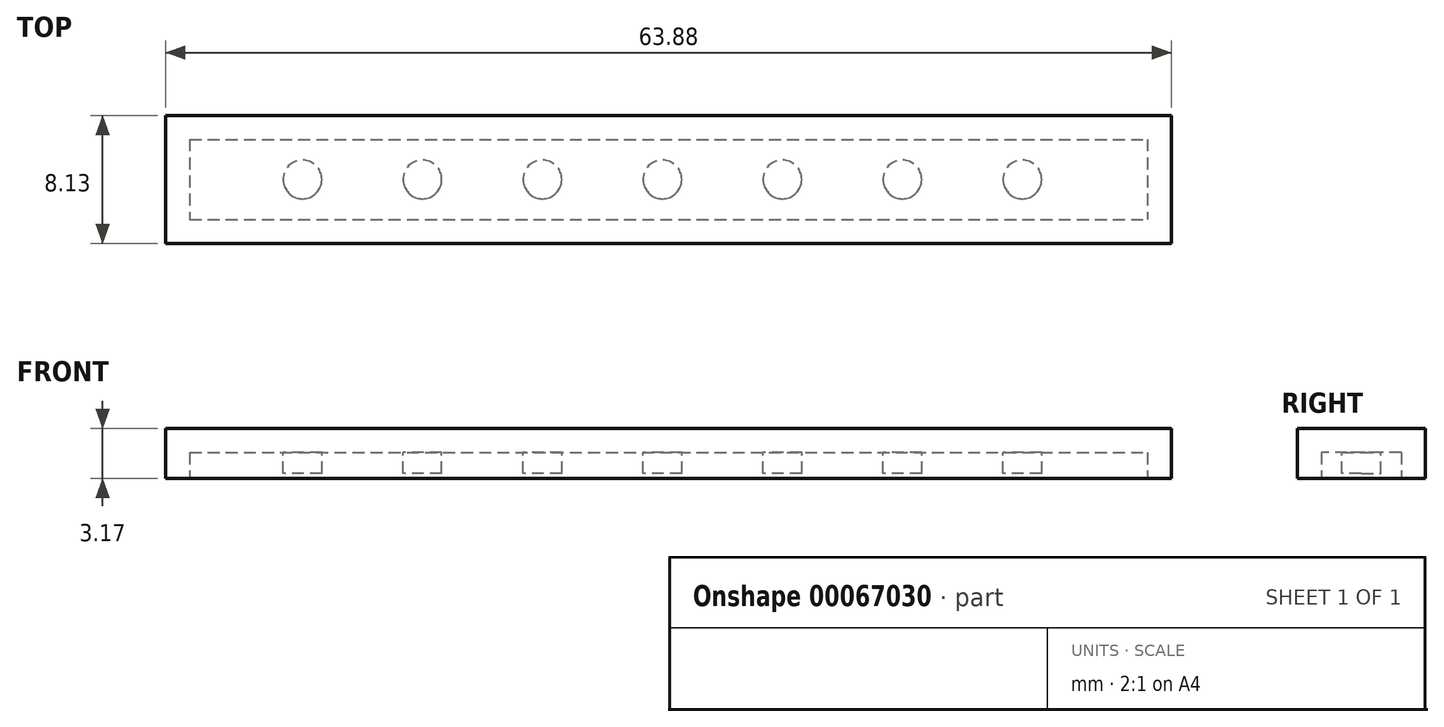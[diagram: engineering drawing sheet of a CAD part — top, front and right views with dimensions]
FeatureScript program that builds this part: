
annotation { "Feature Type Name" : "Feature", "Feature Type Description" : "" }
export const myFeature = defineFeature(function(context is Context, id is Id, definition is map)
    precondition{}
    {
        {
            var Q0;
            Q0=qCreatedBy(makeId("Top.planeOp"),FACE);
            var sketch = newSketch(context, id + "F0", { "sketchPlane" : qUnion([Q0])});
            skLineSegment(sketch, "E0.bottom", {"start": v(-26.06, 4.42) * mm, "end": v(37.82, 4.42) * mm});
            skLineSegment(sketch, "E0.top", {"start": v(-26.06, -3.7) * mm, "end": v(37.82, -3.7) * mm});
            skLineSegment(sketch, "E0.left", {"start": v(-26.06, 4.42) * mm, "end": v(-26.06, -3.7) * mm});
            skLineSegment(sketch, "E0.right", {"start": v(37.82, 4.42) * mm, "end": v(37.82, -3.7) * mm});
            skSolve(sketch);
        }
        {
            var Q0;
            Q0=makeQuery(id+"F0.imprint","IMPRINT",FACE,{"disambiguationData":[TD([[makeQuery(id+"F0.imprint","IMPRINT",EDGE,{"derivedFrom":sQuery(id+"F0.wireOp",EDGE,"E0.bottom")}),-1.0]])]});
            extrude(context, id + "F1", {"entities" : qUnion([Q0]), "depth" : 3.17 * mm});
        }
        {
            var Q0;
            Q0=makeQuery(id+"F1.opExtrude","CAP_FACE",FACE,{"disambiguationData":[OSD([sQuery(id+"F0.wireOp",EDGE,"E0.bottom"),sQuery(id+"F0.wireOp",EDGE,"E0.top"),sQuery(id+"F0.wireOp",EDGE,"E0.left"),sQuery(id+"F0.wireOp",EDGE,"E0.right")])],"isStart":true});
            shell(context, id + "F2", {"entities" : qUnion([Q0]), "thickness" : 1.52 * mm});
        }
        {
            var Q0;
            Q0=makeQuery(id+"F2.opShell","OFFSET_FACE",FACE,{"disambiguationData":[OSD([sQuery(id+"F0.wireOp",EDGE,"E0.bottom"),sQuery(id+"F0.wireOp",EDGE,"E0.top"),sQuery(id+"F0.wireOp",EDGE,"E0.left"),sQuery(id+"F0.wireOp",EDGE,"E0.right")])]});
            var sketch = newSketch(context, id + "F3", { "sketchPlane" : qUnion([Q0])});
            skLineSegment(sketch, "E1", {"start": v(-24.53, -0.36) * mm, "end": v(-17.37, -0.36) * mm});
            skCircle(sketch, "E2", {"center": v(-17.37, -0.36) * mm, "radius": 1.23 * mm});
            skCircle(sketch, "E3.1.0.0", {"center": v(-9.75, -0.36) * mm, "radius": 1.23 * mm});
            skCircle(sketch, "E3.2.0.0", {"center": v(-2.13, -0.36) * mm, "radius": 1.23 * mm});
            skCircle(sketch, "E3.3.0.0", {"center": v(5.49, -0.36) * mm, "radius": 1.23 * mm});
            skCircle(sketch, "E3.4.0.0", {"center": v(13.1, -0.36) * mm, "radius": 1.23 * mm});
            skCircle(sketch, "E3.5.0.0", {"center": v(20.73, -0.36) * mm, "radius": 1.23 * mm});
            skCircle(sketch, "E3.6.0.0", {"center": v(28.35, -0.36) * mm, "radius": 1.23 * mm});
            skLineSegment(sketch, "E3.direction1", {"start": v(-17.37, -0.36) * mm, "end": v(-9.75, -0.36) * mm, "construction": true});
            skSolve(sketch);
        }
        {
            var Q0;
            Q0=makeQuery(id+"F3.imprint","IMPRINT",FACE,{"disambiguationData":[TD([[makeQuery(id+"F3.imprint","IMPRINT",EDGE,{"derivedFrom":sQuery(id+"F3.wireOp",EDGE,"E3.6.0.0")}),1.0]])]});
            var Q1;
            Q1=makeQuery(id+"F3.imprint","IMPRINT",FACE,{"disambiguationData":[TD([[makeQuery(id+"F3.imprint","IMPRINT",EDGE,{"derivedFrom":sQuery(id+"F3.wireOp",EDGE,"E3.5.0.0")}),1.0]])]});
            var Q2;
            Q2=makeQuery(id+"F3.imprint","IMPRINT",FACE,{"disambiguationData":[TD([[makeQuery(id+"F3.imprint","IMPRINT",EDGE,{"derivedFrom":sQuery(id+"F3.wireOp",EDGE,"E3.4.0.0")}),1.0]])]});
            var Q3;
            Q3=makeQuery(id+"F3.imprint","IMPRINT",FACE,{"disambiguationData":[TD([[makeQuery(id+"F3.imprint","IMPRINT",EDGE,{"derivedFrom":sQuery(id+"F3.wireOp",EDGE,"E3.3.0.0")}),1.0]])]});
            var Q4;
            Q4=makeQuery(id+"F3.imprint","IMPRINT",FACE,{"disambiguationData":[TD([[makeQuery(id+"F3.imprint","IMPRINT",EDGE,{"derivedFrom":sQuery(id+"F3.wireOp",EDGE,"E3.2.0.0")}),1.0]])]});
            var Q5;
            Q5=makeQuery(id+"F3.imprint","IMPRINT",FACE,{"disambiguationData":[TD([[makeQuery(id+"F3.imprint","IMPRINT",EDGE,{"derivedFrom":sQuery(id+"F3.wireOp",EDGE,"E3.1.0.0")}),1.0]])]});
            var Q6;
            Q6=makeQuery(id+"F3.imprint","IMPRINT",FACE,{"disambiguationData":[TD([[makeQuery(id+"F3.imprint","IMPRINT",EDGE,{"derivedFrom":sQuery(id+"F3.wireOp",EDGE,"E2")}),1.0]])]});
            extrude(context, id + "F4", {"entities" : qUnion([Q0, Q1, Q2, Q3, Q4, Q5, Q6]), "operationType" : NewBodyOperationType.ADD, "depth" : 1.33 * mm});
        }
    });
